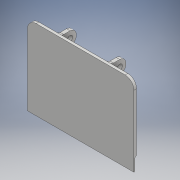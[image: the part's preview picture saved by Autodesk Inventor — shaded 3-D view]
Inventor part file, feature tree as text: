
AUTODESK INVENTOR PART (.ipt)
format: ipt  version: 2017 (Build 210142000, 142)  size: 214,528 bytes
history: native  units: mm
features: fillet x6, projected_geometry x5, sketch x4, extrude x3, hole x1
ambient origin geometry x8: Origin, YZ Plane, XZ Plane, XY Plane, X Axis, Y Axis, Z Axis, Center Point
bodies: Solid1 (feature_tree)
feature tree (19):
  extrude  "Extrusion1"  Depth=90.0mm
  fillet  "Fillet1"  Radius=1.0mm
  extrude  "Extrusion2"  Depth=10.0mm
  fillet  "Fillet2"  Radius=15.0mm
  fillet  "Fillet3"  Radius=2.0mm
  extrude  "Extrusion3"  Depth=55.0mm
  fillet  "Fillet4"  Radius=2.0mm
  fillet  "Fillet5"  Radius=2.0mm
  hole  "Hole1"  [1 undecoded]
  fillet  "Fillet6"  Radius=15.0mm
  sketch  "Sketch1"  dims[d0=120.0mm d1=90.0mm d2=1.0mm d3=0.0mm]
  sketch  "Sketch2"  dims[d4=10.0mm d5=2.0mm d6=15.0mm d7=2.0mm]
  projected_geometry  "Projected Loop1"
  sketch  "Sketch3"  dims[d8=60.0mm d9=55.0mm d10=2.0mm d11=0.0mm d12=2.0mm]
  projected_geometry  "Projected Loop2"
  projected_geometry  "Projected Loop3"
  projected_geometry  "Projected Loop4"
  sketch  "Sketch4"  dims[d13=1.0mm d14=4.0mm d15=15.0mm d16=4.0mm d17=15.0mm d18=20.0mm d19=0.0mm d20=7.0mm d21=5.0mm d23=6.0mm d24=6.0mm d25=4.0mm d26=2.0mm d27=90.0deg d28=8.0mm d29=0.0mm d30=5.0mm]
  projected_geometry  "Projected Loop5"
note: 1 required parameter value undecoded (feature->parameter linkage not recoverable at this tier; creation-order binding heuristic only, values carry confidence <= 0.55)
